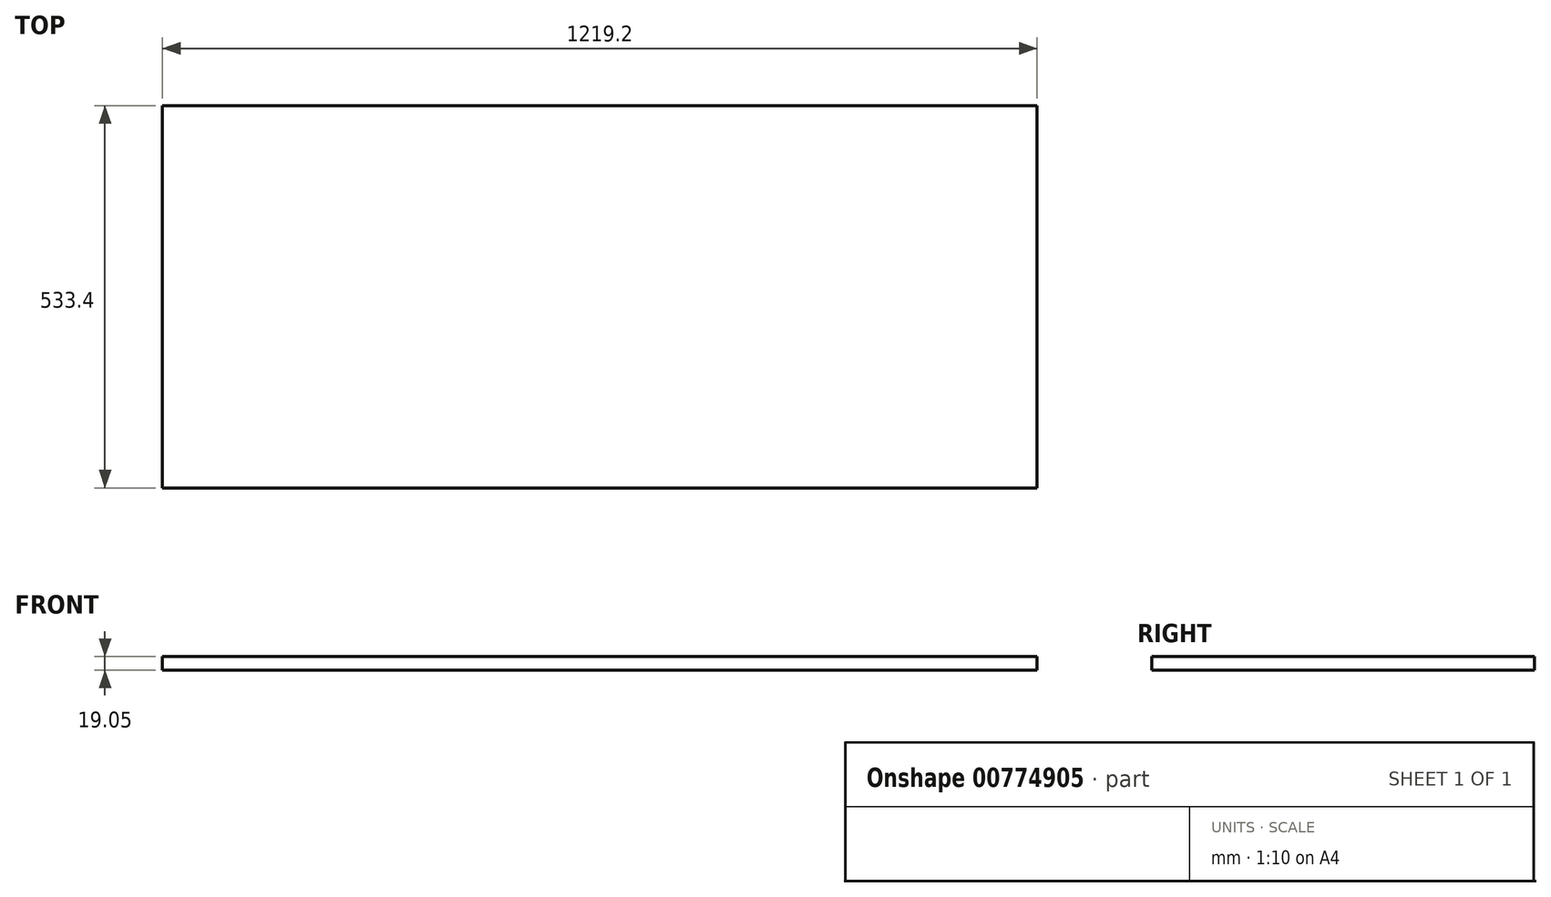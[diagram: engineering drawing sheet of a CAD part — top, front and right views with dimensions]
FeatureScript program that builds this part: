
annotation { "Feature Type Name" : "Feature", "Feature Type Description" : "" }
export const myFeature = defineFeature(function(context is Context, id is Id, definition is map)
    precondition{}
    {
        {
            var Q0;
            Q0=qCreatedBy(makeId("Top.planeOp"),FACE);
            var sketch = newSketch(context, id + "F0", { "sketchPlane" : qUnion([Q0])});
            skLineSegment(sketch, "E0.bottom", {"start": v(609.6, 266.7) * mm, "end": v(-609.6, 266.7) * mm});
            skLineSegment(sketch, "E0.top", {"start": v(609.6, -266.7) * mm, "end": v(-609.6, -266.7) * mm});
            skLineSegment(sketch, "E0.left", {"start": v(609.6, 266.7) * mm, "end": v(609.6, -266.7) * mm});
            skLineSegment(sketch, "E0.right", {"start": v(-609.6, 266.7) * mm, "end": v(-609.6, -266.7) * mm});
            skPoint(sketch, "E0.middle", {"position": v(0, 0) * mm});
            skSolve(sketch);
        }
        {
            var Q0;
            Q0=makeQuery(id+"F0.imprint","IMPRINT",FACE,{"disambiguationData":[TD([[makeQuery(id+"F0.imprint","IMPRINT",EDGE,{"derivedFrom":sQuery(id+"F0.wireOp",EDGE,"E0.bottom")}),1.0]])]});
            extrude(context, id + "F1", {"entities" : qUnion([Q0]), "depth" : 19.05 * mm, "offsetDistance" : 25.4 * mm});
        }
    });
